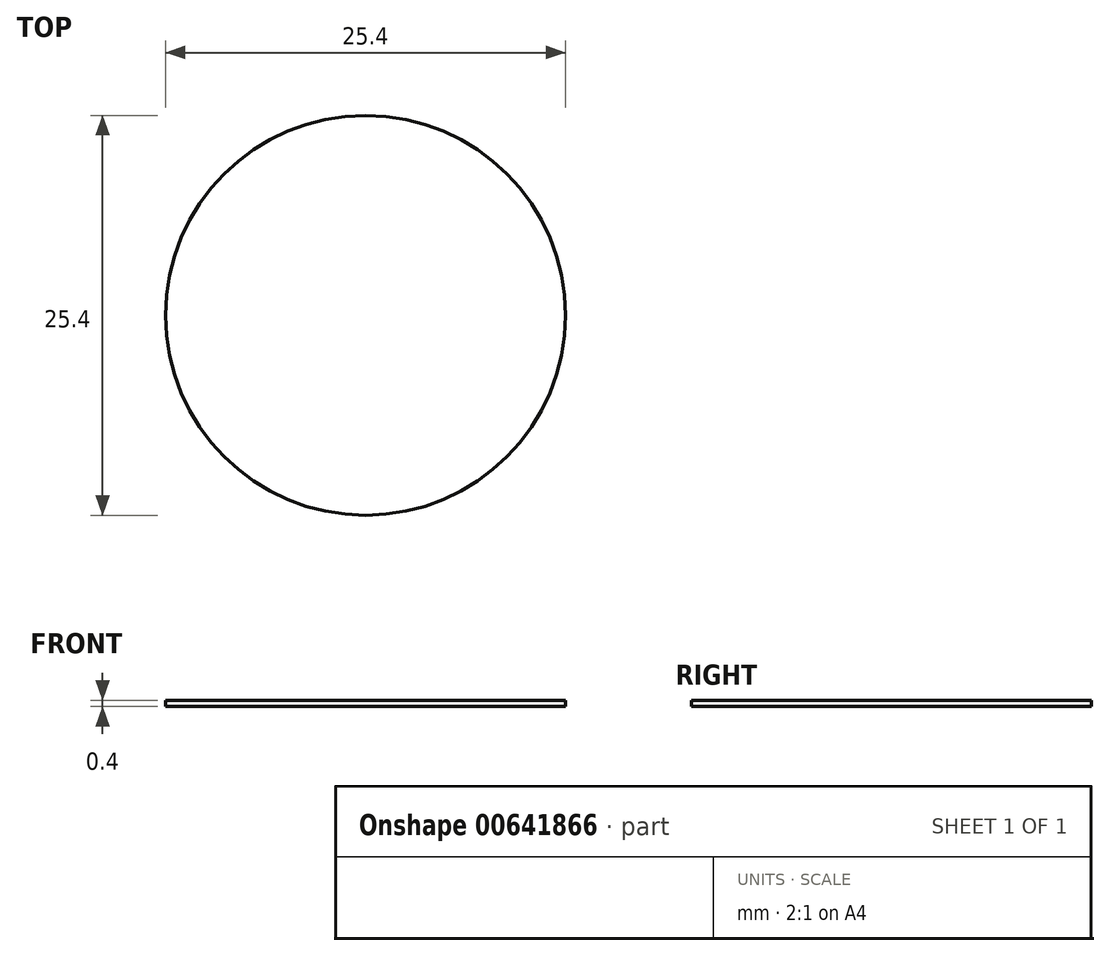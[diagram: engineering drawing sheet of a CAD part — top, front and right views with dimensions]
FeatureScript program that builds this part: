
annotation { "Feature Type Name" : "Feature", "Feature Type Description" : "" }
export const myFeature = defineFeature(function(context is Context, id is Id, definition is map)
    precondition{}
    {
        {
            var Q0;
            Q0=qCreatedBy(makeId("Top.planeOp"),FACE);
            var sketch = newSketch(context, id + "F0", { "sketchPlane" : qUnion([Q0])});
            skCircle(sketch, "E0", {"center": v(0, 0) * mm, "radius": 12.7 * mm});
            skSolve(sketch);
        }
        {
            var Q0;
            Q0=makeQuery(id+"F0.imprint","IMPRINT",FACE,{"disambiguationData":[TD([[makeQuery(id+"F0.imprint","IMPRINT",EDGE,{"derivedFrom":sQuery(id+"F0.wireOp",EDGE,"E0")}),1.0]])]});
            extrude(context, id + "F1", {"entities" : qUnion([Q0]), "depth" : 0.4 * mm, "offsetDistance" : 25.4 * mm});
        }
    });
